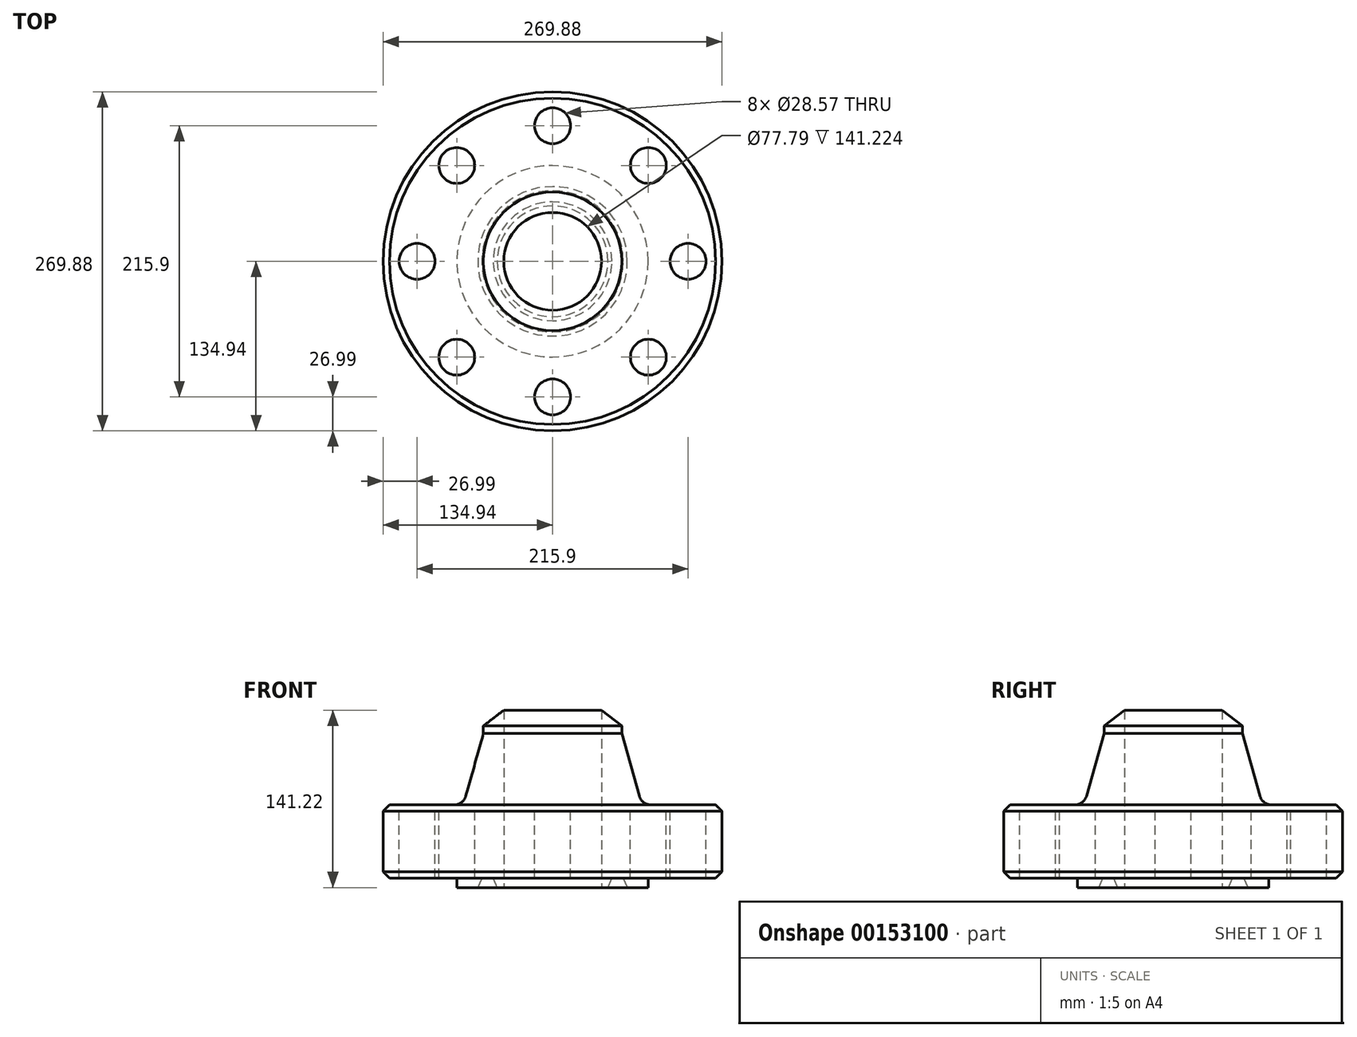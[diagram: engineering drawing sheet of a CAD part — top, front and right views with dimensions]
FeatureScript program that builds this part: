
annotation { "Feature Type Name" : "Feature", "Feature Type Description" : "" }
export const myFeature = defineFeature(function(context is Context, id is Id, definition is map)
    precondition{}
    {
        {
            var Q0;
            Q0=qCreatedBy(makeId("Front.planeOp"),FACE);
            var sketch = newSketch(context, id + "F0", { "sketchPlane" : qUnion([Q0])});
            skLineSegment(sketch, "E0", {"start": v(38.9, -31.72) * mm, "end": v(44.1, -31.72) * mm});
            skLineSegment(sketch, "E1", {"start": v(76.2, -31.72) * mm, "end": v(76.2, -24.18) * mm});
            skLineSegment(sketch, "E2", {"start": v(76.2, -24.18) * mm, "end": v(134.94, -24.18) * mm});
            skLineSegment(sketch, "E3", {"start": v(134.94, -24.18) * mm, "end": v(134.94, 34.16) * mm});
            skLineSegment(sketch, "E4", {"start": v(134.94, 34.16) * mm, "end": v(71.04, 34.16) * mm});
            skLineSegment(sketch, "E5", {"start": v(38.9, -31.72) * mm, "end": v(38.9, 109.5) * mm});
            skLineSegment(sketch, "E6", {"start": v(38.9, 109.5) * mm, "end": v(55.11, 97.06) * mm});
            skLineSegment(sketch, "E7", {"start": v(55.11, 97.06) * mm, "end": v(55.11, 91.06) * mm});
            skLineSegment(sketch, "E8", {"start": v(55.11, 91.06) * mm, "end": v(71.04, 34.16) * mm});
            skLineSegment(sketch, "E9", {"start": v(0, 0) * mm, "end": v(0, 157.84) * mm, "construction": true});
            skLineSegment(sketch, "E10", {"start": v(44.1, -31.72) * mm, "end": v(47.3, -24.18) * mm});
            skLineSegment(sketch, "E11", {"start": v(47.3, -24.18) * mm, "end": v(56.3, -24.18) * mm});
            skLineSegment(sketch, "E12", {"start": v(56.3, -24.18) * mm, "end": v(59.5, -31.72) * mm});
            skLineSegment(sketch, "E13.trimOffspring", {"start": v(59.5, -31.72) * mm, "end": v(76.2, -31.72) * mm});
            skSolve(sketch);
        }
        {
            var Q0;
            Q0=makeQuery(id+"F0.imprint","IMPRINT",FACE,{"disambiguationData":[TD([[makeQuery(id+"F0.imprint","IMPRINT",EDGE,{"derivedFrom":sQuery(id+"F0.wireOp",EDGE,"E0")}),1.0]])]});
            var Q1;
            Q1=sQuery(id+"F0.wireOp",EDGE,"E9");
            revolve(context, id + "F1", {"entities" : qUnion([Q0]), "axis" : qUnion([Q1]), "revolveType" : RevolveType.FULL});
        }
        {
            var Q0;
            Q0=makeQuery(id+"F1.opRevolve","SWEPT_FACE",FACE,{"disambiguationData":[OSD([sQuery(id+"F0.wireOp",EDGE,"E4")])]});
            var sketch = newSketch(context, id + "F2", { "sketchPlane" : qUnion([Q0])});
            skLineSegment(sketch, "E14", {"start": v(0, 0) * mm, "end": v(107.95, 0) * mm, "construction": true});
            skPoint(sketch, "E15", {"position": v(107.95, 0) * mm});
            skPoint(sketch, "E16.1.0", {"position": v(76.33, 76.33) * mm});
            skPoint(sketch, "E16.2.0", {"position": v(0, 107.95) * mm});
            skPoint(sketch, "E16.3.0", {"position": v(-76.33, 76.33) * mm});
            skPoint(sketch, "E16.4.0", {"position": v(-107.95, 0) * mm});
            skPoint(sketch, "E16.5.0", {"position": v(-76.33, -76.33) * mm});
            skPoint(sketch, "E16.6.0", {"position": v(0, -107.95) * mm});
            skPoint(sketch, "E16.7.0", {"position": v(76.33, -76.33) * mm});
            skPoint(sketch, "E16.center", {"position": v(0, 0) * mm});
            skSolve(sketch);
        }
        {
            var Q0;
            Q0=sQuery(id+"F2.wireOp",VERTEX,"E16.2.0");
            var Q1;
            Q1=sQuery(id+"F2.wireOp",VERTEX,"E16.1.0");
            var Q2;
            Q2=sQuery(id+"F2.wireOp",VERTEX,"E15");
            var Q3;
            Q3=sQuery(id+"F2.wireOp",VERTEX,"E16.7.0");
            var Q4;
            Q4=sQuery(id+"F2.wireOp",VERTEX,"E16.6.0");
            var Q5;
            Q5=sQuery(id+"F2.wireOp",VERTEX,"E16.5.0");
            var Q6;
            Q6=sQuery(id+"F2.wireOp",VERTEX,"E16.4.0");
            var Q7;
            Q7=sQuery(id+"F2.wireOp",VERTEX,"E16.3.0");
            var Q8;
            Q8=makeQuery(id+"F1.opRevolve","SWEPT_BODY",BODY,{"disambiguationData":[OSD([sQuery(id+"F0.wireOp",EDGE,"E0"),sQuery(id+"F0.wireOp",EDGE,"E1"),sQuery(id+"F0.wireOp",EDGE,"E2"),sQuery(id+"F0.wireOp",EDGE,"E3"),sQuery(id+"F0.wireOp",EDGE,"E4"),sQuery(id+"F0.wireOp",EDGE,"E5"),sQuery(id+"F0.wireOp",EDGE,"E6"),sQuery(id+"F0.wireOp",EDGE,"E7"),sQuery(id+"F0.wireOp",EDGE,"E8"),sQuery(id+"F0.wireOp",EDGE,"E10"),sQuery(id+"F0.wireOp",EDGE,"E11"),sQuery(id+"F0.wireOp",EDGE,"E12"),sQuery(id+"F0.wireOp",EDGE,"E13.trimOffspring")])]});
            hole(context, id + "F3", {"style" : HoleStyle.SIMPLE, "endStyle" : HoleEndStyle.THROUGH, "holeDiameter" : 28.57 * mm, "locations" : qUnion([Q0, Q1, Q2, Q3, Q4, Q5, Q6, Q7]), "scope" : qUnion([Q8]), "isTappedThrough" : true});
        }
        {
            var Q0;
            Q0=makeQuery(id+"F1.opRevolve","SWEPT_EDGE",EDGE,{"disambiguationData":[OSD([sQuery(id+"F0.wireOp",EDGE,"E4"),sQuery(id+"F0.wireOp",EDGE,"E8")])]});
            fillet(context, id + "F4", {"entities" : qUnion([Q0]), "radius" : 9.52 * mm, "tangentPropagation" : true, "allowEdgeOverflow" : false});
        }
        {
            var Q0;
            Q0=makeQuery(id+"F1.opRevolve","SWEPT_EDGE",EDGE,{"disambiguationData":[OSD([sQuery(id+"F0.wireOp",EDGE,"E2"),sQuery(id+"F0.wireOp",EDGE,"E3")])]});
            chamfer(context, id + "F5", {"entities" : qUnion([Q0]), "width" : 5 * mm, "tangentPropagation" : true});
        }
        {
            var Q0;
            Q0=makeQuery(id+"F1.opRevolve","SWEPT_EDGE",EDGE,{"disambiguationData":[OSD([sQuery(id+"F0.wireOp",EDGE,"E3"),sQuery(id+"F0.wireOp",EDGE,"E4")])]});
            chamfer(context, id + "F6", {"entities" : qUnion([Q0]), "width" : 5 * mm, "tangentPropagation" : true});
        }
    });
